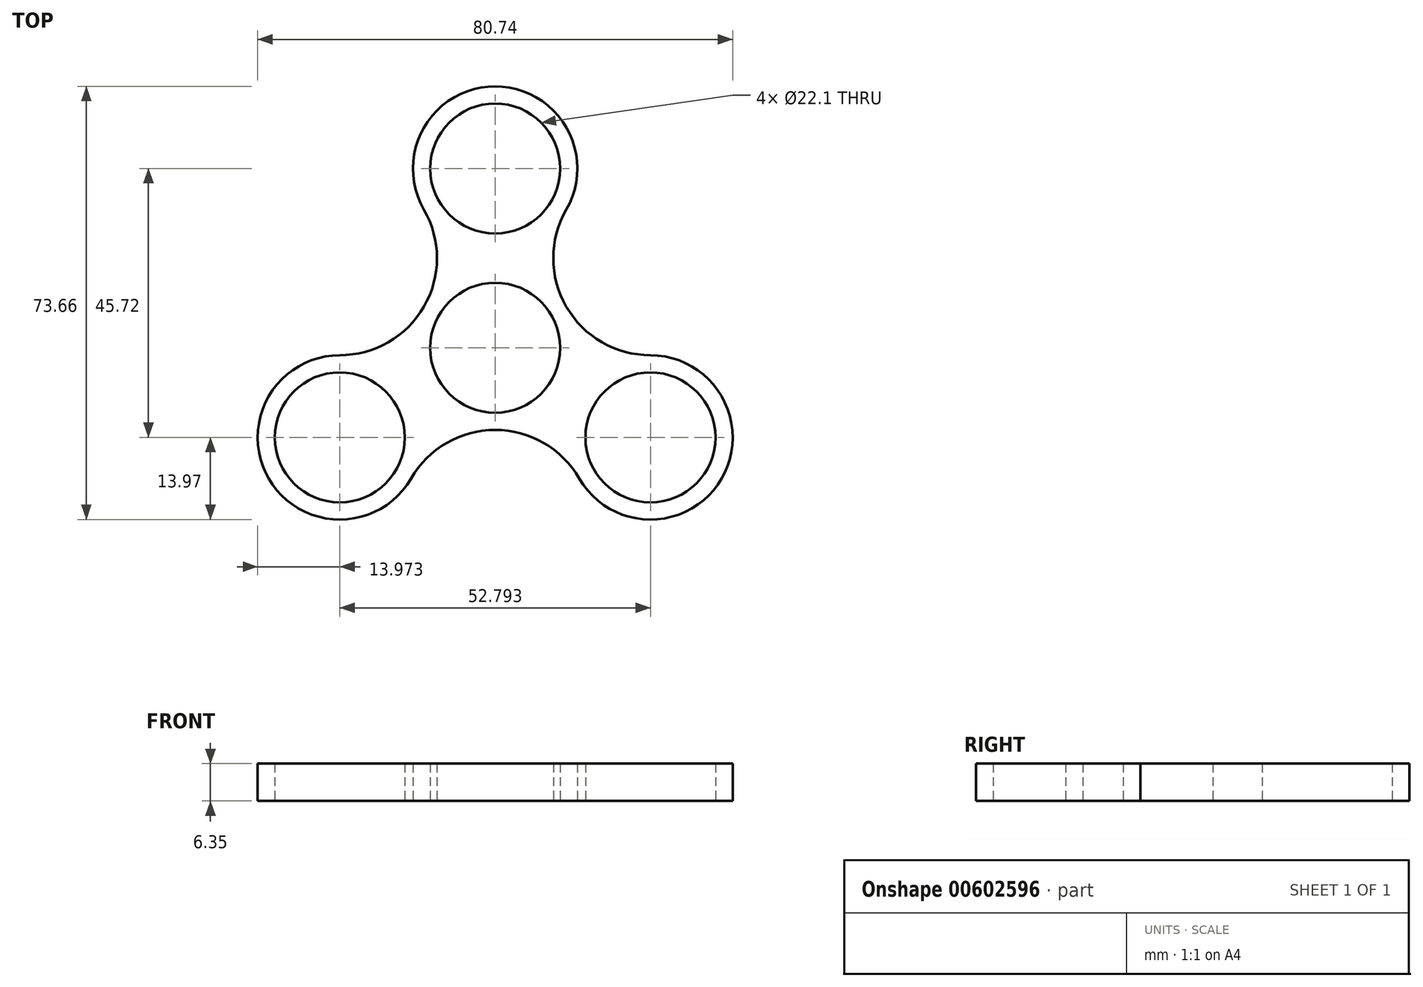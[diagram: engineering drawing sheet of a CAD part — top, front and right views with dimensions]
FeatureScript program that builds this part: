
annotation { "Feature Type Name" : "Feature", "Feature Type Description" : "" }
export const myFeature = defineFeature(function(context is Context, id is Id, definition is map)
    precondition{}
    {
        {
            var Q0;
            Q0=qCreatedBy(makeId("Top.planeOp"),FACE);
            var sketch = newSketch(context, id + "F0", { "sketchPlane" : qUnion([Q0])});
            skCircle(sketch, "E0", {"center": v(0, 0) * mm, "radius": 11.05 * mm});
            skCircle(sketch, "E1", {"center": v(0, 0) * mm, "radius": 13.97 * mm});
            skLineSegment(sketch, "E2", {"start": v(0, 0) * mm, "end": v(0, 30.48) * mm});
            skCircle(sketch, "E3", {"center": v(0, 30.48) * mm, "radius": 11.05 * mm});
            skCircle(sketch, "E4", {"center": v(0, 30.48) * mm, "radius": 13.97 * mm});
            skCircle(sketch, "E5.1.0", {"center": v(-26.4, -15.24) * mm, "radius": 13.97 * mm});
            skCircle(sketch, "E5.1.1", {"center": v(-26.4, -15.24) * mm, "radius": 11.05 * mm});
            skCircle(sketch, "E5.2.0", {"center": v(26.4, -15.24) * mm, "radius": 13.97 * mm});
            skCircle(sketch, "E5.2.1", {"center": v(26.4, -15.24) * mm, "radius": 11.05 * mm});
            skCircle(sketch, "E6", {"center": v(0, 0) * mm, "radius": 44.45 * mm});
            skLineSegment(sketch, "E7", {"start": v(0, 0) * mm, "end": v(-26.4, 15.24) * mm});
            skArc(sketch, "E8", {"start": v(-26.4, -1.27) * mm, "mid": v(-12.1, 6.99) * mm, "end": v(-12.1, 23.5) * mm});
            skLineSegment(sketch, "E9", {"start": v(0, 0) * mm, "end": v(26.4, 15.24) * mm});
            skArc(sketch, "E10", {"start": v(12.1, 23.5) * mm, "mid": v(12.1, 6.99) * mm, "end": v(26.4, -1.27) * mm});
            skLineSegment(sketch, "E11", {"start": v(0, 0) * mm, "end": v(1.71, -2.97) * mm});
            skArc(sketch, "E12.1.0", {"start": v(14.3, -22.23) * mm, "mid": v(0, -13.97) * mm, "end": v(-14.3, -22.22) * mm});
            skArc(sketch, "E12.2.0", {"start": v(12.1, 23.5) * mm, "mid": v(12.1, 6.98) * mm, "end": v(26.4, -1.27) * mm});
            skSolve(sketch);
        }
        {
            var Q0;
            Q0=makeQuery(id+"F0.imprint","IMPRINT",FACE,{"disambiguationData":[TD([[makeQuery(id+"F0.imprint","IMPRINT",EDGE,{"derivedFrom":sQuery(id+"F0.wireOp",EDGE,"E5.1.1")}),-1.0]])]});
            var Q1;
            {var subQ3=sQuery(id+"F0.wireOp",EDGE,"E8");var subQ5=sQuery(id+"F0.wireOp",EDGE,"E5.1.0");var subQ6=makeQuery(id+"F0.imprint","INTERSECT",VERTEX,{"derivedFrom":[subQ5,subQ3]});Q1=makeQuery(id+"F0.imprint","IMPRINT",FACE,{"disambiguationData":[TD([[makeQuery(id+"F0.imprint","IMPRINT",EDGE,{"disambiguationData":[TD([[subQ6,1.0]])],"derivedFrom":subQ5}),-1.0]])]});}
            var Q2;
            {var subQ0=sQuery(id+"F0.wireOp",EDGE,"E12.1.0");var subQ5=sQuery(id+"F0.wireOp",EDGE,"E5.2.0");var subQ6=makeQuery(id+"F0.imprint","INTERSECT",VERTEX,{"derivedFrom":[subQ5,subQ0]});Q2=makeQuery(id+"F0.imprint","IMPRINT",FACE,{"disambiguationData":[TD([[makeQuery(id+"F0.imprint","IMPRINT",EDGE,{"disambiguationData":[TD([[subQ6,1.0]])],"derivedFrom":subQ5}),-1.0]])]});}
            var Q3;
            {var subQ0=sQuery(id+"F0.wireOp",EDGE,"E2");var subQ5=sQuery(id+"F0.wireOp",EDGE,"E4");var subQ7=makeQuery(id+"F0.imprint","INTERSECT",VERTEX,{"derivedFrom":[subQ0,subQ5]});Q3=makeQuery(id+"F0.imprint","IMPRINT",FACE,{"disambiguationData":[TD([[makeQuery(id+"F0.imprint","IMPRINT",EDGE,{"disambiguationData":[TD([[subQ7,1.0]])],"derivedFrom":subQ0}),-1.0]])]});}
            var Q4;
            {var subQ0=sQuery(id+"F0.wireOp",EDGE,"E2");var subQ5=sQuery(id+"F0.wireOp",EDGE,"E4");var subQ6=makeQuery(id+"F0.imprint","INTERSECT",VERTEX,{"derivedFrom":[subQ0,subQ5]});Q4=makeQuery(id+"F0.imprint","IMPRINT",FACE,{"disambiguationData":[TD([[makeQuery(id+"F0.imprint","IMPRINT",EDGE,{"disambiguationData":[TD([[subQ6,1.0]])],"derivedFrom":subQ0}),1.0]])]});}
            var Q5;
            {var subQ0=sQuery(id+"F0.wireOp",EDGE,"E2");var subQ1=sQuery(id+"F0.wireOp",EDGE,"E0");var subQ2=makeQuery(id+"F0.imprint","INTERSECT",VERTEX,{"derivedFrom":[subQ1,subQ0]});Q5=makeQuery(id+"F0.imprint","IMPRINT",FACE,{"disambiguationData":[TD([[makeQuery(id+"F0.imprint","IMPRINT",EDGE,{"disambiguationData":[TD([[subQ2,-1.0]])],"derivedFrom":subQ1}),-1.0]])]});}
            var Q6;
            {var subQ0=sQuery(id+"F0.wireOp",EDGE,"E2");var subQ1=sQuery(id+"F0.wireOp",EDGE,"E0");var subQ2=makeQuery(id+"F0.imprint","INTERSECT",VERTEX,{"derivedFrom":[subQ1,subQ0]});Q6=makeQuery(id+"F0.imprint","IMPRINT",FACE,{"disambiguationData":[TD([[makeQuery(id+"F0.imprint","IMPRINT",EDGE,{"disambiguationData":[TD([[subQ2,1.0]])],"derivedFrom":subQ1}),-1.0]])]});}
            var Q7;
            {var subQ2=sQuery(id+"F0.wireOp",EDGE,"E9");var subQ6=sQuery(id+"F0.wireOp",EDGE,"E0");var subQ8=makeQuery(id+"F0.imprint","INTERSECT",VERTEX,{"derivedFrom":[subQ6,subQ2]});Q7=makeQuery(id+"F0.imprint","IMPRINT",FACE,{"disambiguationData":[TD([[makeQuery(id+"F0.imprint","IMPRINT",EDGE,{"disambiguationData":[TD([[subQ8,1.0]])],"derivedFrom":subQ6}),-1.0]])]});}
            var Q8;
            Q8=makeQuery(id+"F0.imprint","IMPRINT",FACE,{"disambiguationData":[TD([[makeQuery(id+"F0.imprint","IMPRINT",EDGE,{"derivedFrom":sQuery(id+"F0.wireOp",EDGE,"E3")}),-1.0]])]});
            var Q9;
            Q9=makeQuery(id+"F0.imprint","IMPRINT",FACE,{"disambiguationData":[TD([[makeQuery(id+"F0.imprint","IMPRINT",EDGE,{"derivedFrom":sQuery(id+"F0.wireOp",EDGE,"E5.2.1")}),-1.0]])]});
            extrude(context, id + "F1", {"entities" : qUnion([Q0, Q1, Q2, Q3, Q4, Q5, Q6, Q7, Q8, Q9]), "depth" : 6.35 * mm, "offsetDistance" : 25.4 * mm});
        }
    });
